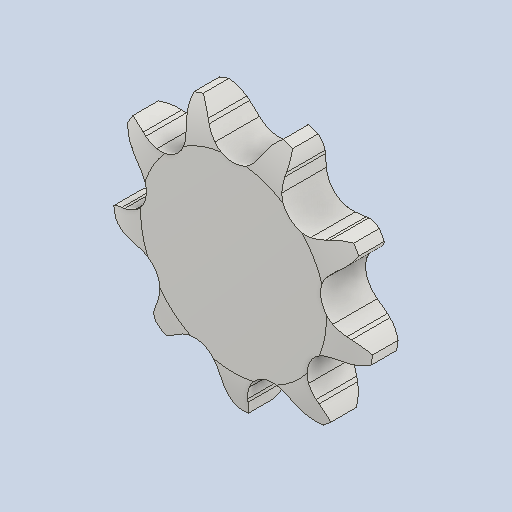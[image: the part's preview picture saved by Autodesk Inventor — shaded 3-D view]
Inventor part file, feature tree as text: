
AUTODESK INVENTOR PART (.ipt)
format: ipt  version: 2022.1 (Build 261234000, 234)  size: 372,224 bytes
history: native  units: mm
features: other x6, extrude x2, pattern_linear x1, pattern_circular x1
ambient origin geometry x8: Origin, YZ Plane, XZ Plane, XY Plane, X Axis, Y Axis, Z Axis, Center Point
bodies: Solid1 (feature_tree)
feature tree (10):
  other  "Perfil de diente teórico"
  other  "Perfil de diente"
  other  "Perfil de sección"
  other  "Cubierta"
  other  "Ramal"
  pattern_linear  "Patrón de ramal"  Spacing1=46.415395mm  [1 undecoded]
  extrude  "Diente teórico"  Depth=6.981317mm
  extrude  "Diente"  Depth=5.1308mm
  pattern_circular  "Patrón de diente"  [2 undecoded]
  other  "Plano síncrono"
note: 3 required parameter values undecoded (feature->parameter linkage not recoverable at this tier; creation-order binding heuristic only, values carry confidence <= 0.55)
